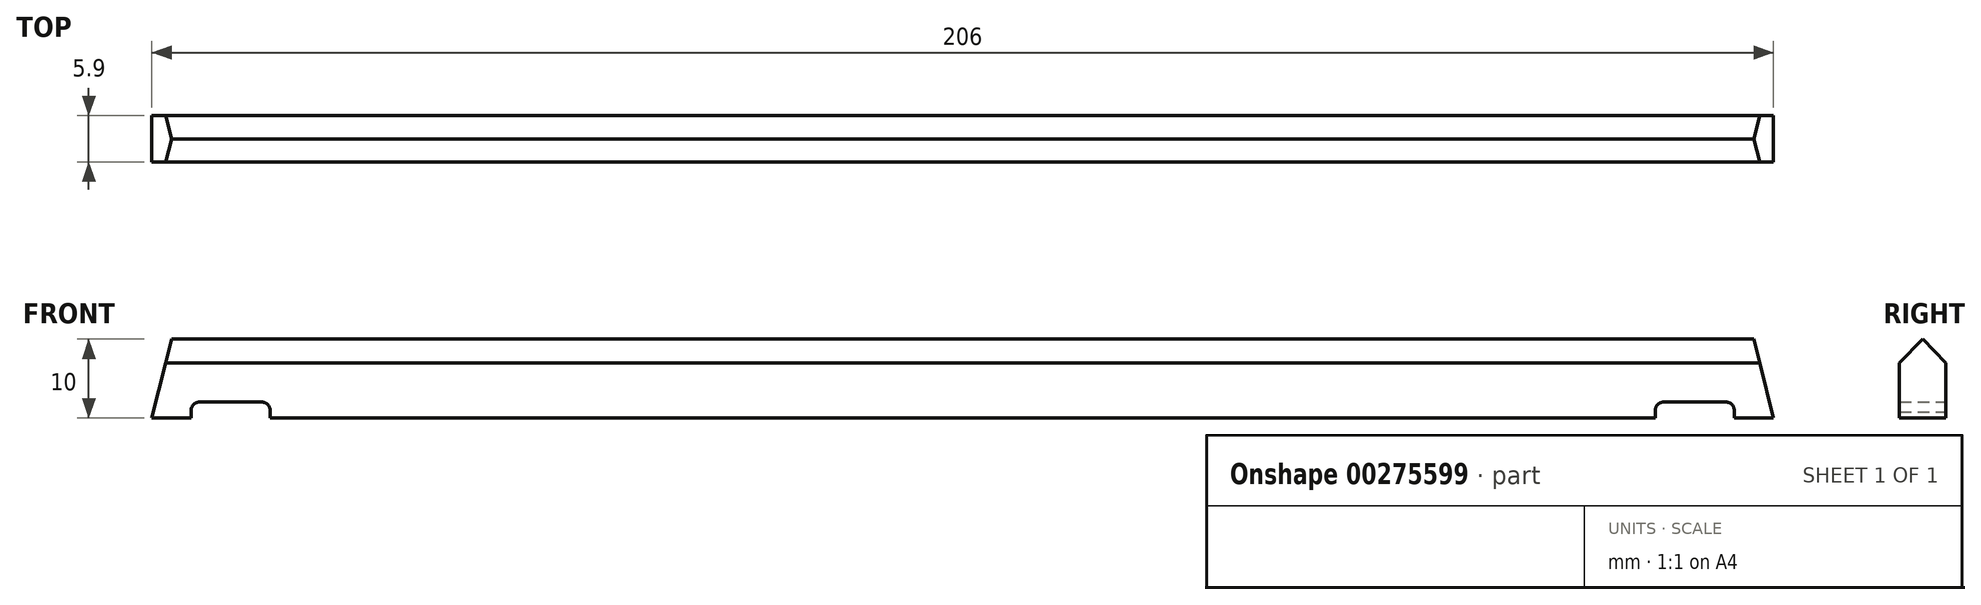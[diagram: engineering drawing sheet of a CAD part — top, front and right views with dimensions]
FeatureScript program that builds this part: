
annotation { "Feature Type Name" : "Feature", "Feature Type Description" : "" }
export const myFeature = defineFeature(function(context is Context, id is Id, definition is map)
    precondition{}
    {
        {
            var Q0;
            Q0=qCreatedBy(makeId("Front.planeOp"),FACE);
            var sketch = newSketch(context, id + "F0", { "sketchPlane" : qUnion([Q0])});
            skLineSegment(sketch, "E0", {"start": v(0, 0) * mm, "end": v(-5, 0) * mm});
            skLineSegment(sketch, "E1", {"start": v(-103, 0) * mm, "end": v(-103, 18.32) * mm, "construction": true});
            skLineSegment(sketch, "E2", {"start": v(-103, 10) * mm, "end": v(-203.5, 10) * mm});
            skLineSegment(sketch, "E3", {"start": v(-103, 10) * mm, "end": v(-2.5, 10) * mm});
            skLineSegment(sketch, "E4", {"start": v(-203.5, 10) * mm, "end": v(-206, 0) * mm});
            skLineSegment(sketch, "E5", {"start": v(-2.5, 10) * mm, "end": v(0, 0) * mm});
            skLineSegment(sketch, "E6", {"start": v(-2.5, 10) * mm, "end": v(7.33, 10) * mm});
            skLineSegment(sketch, "E7", {"start": v(-201, 0) * mm, "end": v(-201, 5.38) * mm, "construction": true});
            skLineSegment(sketch, "E8", {"start": v(-191, 5.38) * mm, "end": v(-191, -2.32) * mm, "construction": true});
            skLineSegment(sketch, "E9", {"start": v(-203.3, 2) * mm, "end": v(-186.7, 2) * mm, "construction": true});
            skLineSegment(sketch, "E10", {"start": v(-200, 3.18) * mm, "end": v(-200, -0.94) * mm, "construction": true});
            skLineSegment(sketch, "E11", {"start": v(-192, 3.34) * mm, "end": v(-192, -1.38) * mm, "construction": true});
            skLineSegment(sketch, "E12", {"start": v(-201.77, 1) * mm, "end": v(-188.15, 1) * mm, "construction": true});
            skArc(sketch, "E13", {"start": v(-200, 2) * mm, "mid": v(-200.7, 1.7) * mm, "end": v(-201, 1) * mm});
            skArc(sketch, "E14.trimOffspring", {"start": v(-191, 0.78) * mm, "mid": v(-191.21, 1.63) * mm, "end": v(-192, 2) * mm});
            skLineSegment(sketch, "E15.trimOffspring", {"start": v(-201, 0) * mm, "end": v(-206, 0) * mm});
            skLineSegment(sketch, "E16", {"start": v(-200, 2) * mm, "end": v(-192, 2) * mm});
            skArc(sketch, "E17.MirrorCS", {"start": v(-6, 2) * mm, "mid": v(-5.3, 1.7) * mm, "end": v(-5, 1) * mm});
            skArc(sketch, "E18.MirrorCS", {"start": v(-15, 0.78) * mm, "mid": v(-14.79, 1.63) * mm, "end": v(-14, 2) * mm});
            skLineSegment(sketch, "E19", {"start": v(-191, 0.78) * mm, "end": v(-191, 0) * mm});
            skLineSegment(sketch, "E20", {"start": v(-201, 1) * mm, "end": v(-201, 0) * mm});
            skLineSegment(sketch, "E21.MirrorCS", {"start": v(-5, 0) * mm, "end": v(-5, 5.38) * mm, "construction": true});
            skLineSegment(sketch, "E22.MirrorCS", {"start": v(-2.7, 2) * mm, "end": v(-19.3, 2) * mm, "construction": true});
            skLineSegment(sketch, "E23.MirrorCS", {"start": v(-15, 5.38) * mm, "end": v(-15, -2.32) * mm, "construction": true});
            skLineSegment(sketch, "E24", {"start": v(-15, 0.78) * mm, "end": v(-15, 0) * mm});
            skLineSegment(sketch, "E25", {"start": v(-14, 2) * mm, "end": v(-6, 2) * mm});
            skLineSegment(sketch, "E26", {"start": v(-5, 1) * mm, "end": v(-5, 0) * mm});
            skLineSegment(sketch, "E27.trimOffspring", {"start": v(-15, 0) * mm, "end": v(-191, 0) * mm});
            skSolve(sketch);
        }
        {
            var Q0;
            Q0=makeQuery(id+"F0.imprint","IMPRINT",FACE,{"disambiguationData":[TD([[makeQuery(id+"F0.imprint","IMPRINT",EDGE,{"derivedFrom":sQuery(id+"F0.wireOp",EDGE,"E0")}),-1.0]])]});
            extrude(context, id + "F1", {"entities" : qUnion([Q0]), "depth" : 5.9 * mm});
        }
        {
            var Q0;
            Q0=qCreatedBy(makeId("Right.planeOp"),FACE);
            var sketch = newSketch(context, id + "F2", { "sketchPlane" : qUnion([Q0])});
            skLineSegment(sketch, "E28", {"start": v(-2.95, 0) * mm, "end": v(-2.95, 12.39) * mm});
            skLineSegment(sketch, "E29", {"start": v(-2.95, 10) * mm, "end": v(-5.9, 10) * mm});
            skLineSegment(sketch, "E30", {"start": v(-2.95, 10) * mm, "end": v(0, 10) * mm});
            skLineSegment(sketch, "E31", {"start": v(-5.9, 10) * mm, "end": v(-5.9, 0) * mm});
            skLineSegment(sketch, "E32", {"start": v(-5.9, 0) * mm, "end": v(0, 0) * mm});
            skLineSegment(sketch, "E33", {"start": v(0, 0) * mm, "end": v(0, 10) * mm});
            skLineSegment(sketch, "E34", {"start": v(-2.95, 10) * mm, "end": v(-5.9, 7) * mm});
            skLineSegment(sketch, "E35", {"start": v(-2.95, 10) * mm, "end": v(0, 7) * mm});
            skSolve(sketch);
        }
        {
            var Q0;
            {var subQ0=sQuery(id+"F2.wireOp",EDGE,"E29");Q0=makeQuery(id+"F2.imprint","IMPRINT",FACE,{"disambiguationData":[TD([[makeQuery(id+"F2.imprint","IMPRINT",EDGE,{"derivedFrom":subQ0}),1.0]])]});}
            var Q1;
            {var subQ0=sQuery(id+"F2.wireOp",EDGE,"E30");Q1=makeQuery(id+"F2.imprint","IMPRINT",FACE,{"disambiguationData":[TD([[makeQuery(id+"F2.imprint","IMPRINT",EDGE,{"derivedFrom":subQ0}),-1.0]])]});}
            extrude(context, id + "F3", {"entities" : qUnion([Q0, Q1]), "operationType" : NewBodyOperationType.REMOVE, "oppositeDirection" : true, "depth" : 300 * mm});
        }
    });
